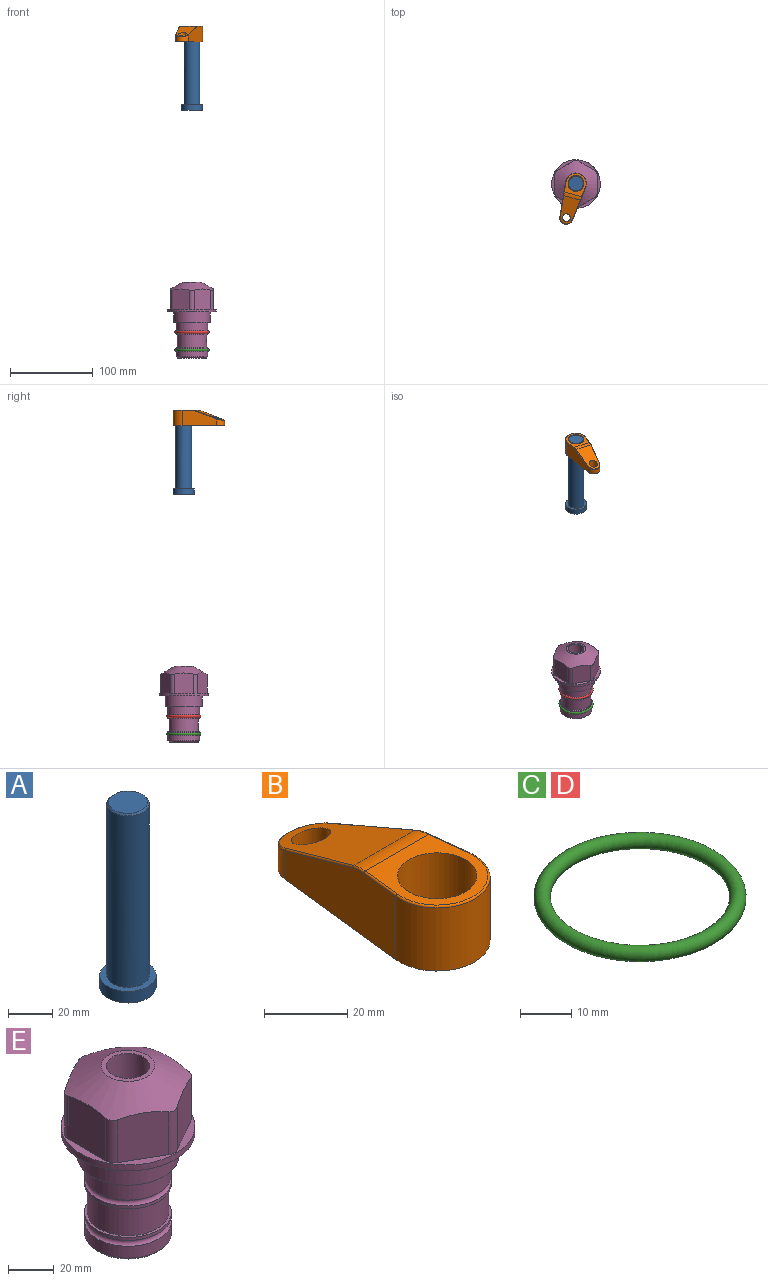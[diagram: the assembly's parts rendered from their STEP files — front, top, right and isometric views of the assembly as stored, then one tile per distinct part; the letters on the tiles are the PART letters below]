
ASSEMBLY  parts=5 mates=3
PART A: 6 faces, bbox 25.4x25.4x101.6 mm
  f0: plane 17.46x17.46mm, normal (0,0,1), area 239.5mm2, adj f5
  f1: plane 25.4x25.4mm, normal (0,0,-1), area 506.7mm2, adj f2
  f2: cylinder r=12.7mm len=25.4mm, axis (0,0,1), area 506.7mm2, adj f1,f3
  f3: plane 25.4x25.4mm, normal (0,0,1), area 221.7mm2, adj f2,f4
  f4: cylinder r=9.53mm len=94.46mm, axis (0,0,1), area 5653mm2, adj f3,f5
  f5: cone r=8.73mm half-angle=45deg, axis (0,0,-1), area 64.4mm2, adj f0,f4
PART B: 44 faces, bbox 27.5x64.5x19.1 mm
  f0: plane 2.3x0.95mm, normal (0,0,-1), area 1mm2, adj f25,f30,f34
  f1: plane 63.5x25.4mm, normal (0,0,-1), area 561.7mm2, adj f2,f3,f4,f5,f6,f7,f19,f20
  f2: cylinder r=12.7mm len=25.4mm, axis (0,0,-1), area 792.2mm2, adj f1,f3,f5,f13
  f3: plane 42.33x18.54mm, normal (0.99,0.11,0), area 647mm2, adj f1,f2,f4,f11,f12,f14
  f4: cylinder r=7.94mm len=15.78mm, axis (0,0,-1), area 158.6mm2, adj f1,f3,f5,f16
  f5: plane 42.33x18.54mm, normal (-0.99,0.11,0), area 647mm2, adj f1,f2,f4,f15,f17,f18
  f6: cylinder r=9.53mm len=19.05mm, axis (0,0,-1), area 1140.1mm2, adj f1,f8
  f7: cylinder r=4.76mm len=10.98mm, axis (0,0,-1), area 276.1mm2, adj f1,f9
  f8: plane 25.83x24.38mm, normal (0,0,1), area 262.2mm2, adj f6,f10,f11,f13,f15
  f9: plane 32.49x20.55mm, normal (0,0.34,0.94), area 489.9mm2, adj f7,f10,f14,f16,f18
  f10: cylinder r=12.7mm len=21.49mm, axis (-1,0,0), area 93.2mm2, adj f8,f9,f12,f17
  f11: cylinder r=0.51mm len=12.34mm, axis (0.11,-0.99,0), area 9.9mm2, adj f3,f8,f12,f13
  f12: bspline ~7.62x1.64mm, area 3.5mm2, adj f3,f10,f11,f14
  f13: torus R=12.19mm, axis (0,0,1), area 33.6mm2, adj f2,f8,f11,f15
  f14: cylinder r=0.51mm len=26.01mm, axis (0.1,-0.93,0.34), area 21.6mm2, adj f3,f9,f12,f16
  f15: cylinder r=0.51mm len=12.34mm, axis (0.11,0.99,0), area 9.9mm2, adj f5,f8,f13,f17
  f16: bspline ~15.78x7.05mm, area 15.7mm2, adj f4,f9,f14,f18
  f17: bspline ~7.62x1.64mm, area 3.5mm2, adj f5,f10,f15,f18
  f18: cylinder r=0.51mm len=26.01mm, axis (0.1,0.93,-0.34), area 21.6mm2, adj f5,f9,f16,f17
  f19: plane 21.6x14.29mm, normal (-0.99,-0.11,0), area 242.6mm2, adj f1,f26,f28,f34,f36,f38
  f20: plane 21.6x14.29mm, normal (0.99,-0.11,0), area 242.6mm2, adj f1,f27,f29,f37,f39,f41
  f21: cylinder r=12.7mm len=14.29mm, axis (0,0,-1), area 173.2mm2, adj f1,f26,f27,f30,f31,f33
  f22: cylinder r=7.94mm len=7.63mm, axis (0,0,-1), area 53.8mm2, adj f1,f28,f29,f42
  f23: plane 2.3x0.95mm, normal (0,0,-1), area 1mm2, adj f25,f33,f37
  f24: plane 17.94x12.32mm, normal (0,-0.34,-0.94), area 191.2mm2, adj f25,f38,f41,f42
  f25: cylinder r=9.53mm len=12.93mm, axis (-1,0,0), area 37.5mm2, adj f0,f23,f24,f31,f36,f39
  f26: cylinder r=1.59mm len=14.29mm, axis (0,0,-1), area 49mm2, adj f1,f19,f21,f32
  f27: cylinder r=1.59mm len=14.29mm, axis (0,0,-1), area 49mm2, adj f1,f20,f21,f35
  f28: cylinder r=1.59mm len=7.28mm, axis (0,0,-1), area 22.1mm2, adj f1,f19,f22,f40
  f29: cylinder r=1.59mm len=7.28mm, axis (0,0,-1), area 22.1mm2, adj f1,f20,f22,f43
  f30: torus R=14.29mm, axis (0,0,1), area 5.8mm2, adj f0,f21,f31,f32
  f31: bspline ~11.06x2.73mm, area 20.8mm2, adj f21,f25,f30,f33
  f32: sphere r=1.59mm, area 5.4mm2, adj f26,f30,f34
  f33: torus R=14.29mm, axis (0,0,1), area 5.8mm2, adj f21,f23,f31,f35
  f34: cylinder r=1.59mm len=1.68mm, axis (-0.11,0.99,0), area 2.4mm2, adj f0,f19,f32,f36
  f35: sphere r=1.59mm, area 5.4mm2, adj f27,f33,f37
  f36: bspline ~5.82x2.33mm, area 7.7mm2, adj f19,f25,f34,f38
  f37: cylinder r=1.59mm len=1.68mm, axis (0.11,0.99,0), area 2.4mm2, adj f20,f23,f35,f39
  f38: cylinder r=1.59mm len=18.33mm, axis (0.1,-0.93,0.34), area 46.7mm2, adj f19,f24,f36,f40
  f39: bspline ~5.82x2.33mm, area 7.7mm2, adj f20,f25,f37,f41
  f40: sphere r=1.59mm, area 3.6mm2, adj f28,f38,f42
  f41: cylinder r=1.59mm len=18.33mm, axis (0.1,0.93,-0.34), area 46.7mm2, adj f20,f24,f39,f43
  f42: bspline ~8.31x1.84mm, area 15.3mm2, adj f22,f24,f40,f43
  f43: sphere r=1.59mm, area 3.6mm2, adj f29,f41,f42
PART C: 1 faces, bbox 44.7x44.7x3.2 mm
  f0: torus R=19.05mm, axis (0,0,1), area 1193.9mm2
PART D: same geometry as C
PART E: 36 faces, bbox 58.7x58.7x91.2 mm
  f0: cylinder r=17.78mm len=35.56mm, axis (0,0,1), area 1670.8mm2, adj f23,f24,f31
  f1: cylinder r=19.05mm len=38.1mm, axis (0,0,1), area 1191.9mm2, adj f26,f27,f30
  f2: plane 58.66x58.66mm, normal (0,0,-1), area 1150.6mm2, adj f3,f28
  f3: cylinder r=29.33mm len=58.66mm, axis (0,0,-1), area 585.1mm2, adj f2,f4
  f4: plane 58.66x58.66mm, normal (0,0,1), area 475.9mm2, adj f3,f5,f6,f7,f8,f9,f10,f11
  f5: plane 24.5x20.32mm, normal (-0.5,0.87,0), area 562.8mm2, adj f4,f15,f16,f17
  f6: plane 24.5x20.32mm, normal (0.5,0.87,0), area 562.8mm2, adj f4,f14,f15,f17
  f7: plane 24.5x23.48mm, normal (1,0,0), area 562.8mm2, adj f4,f13,f14,f17
  f8: plane 24.5x20.32mm, normal (0.5,-0.87,0), area 562.8mm2, adj f4,f12,f13,f17
  f9: plane 24.5x20.32mm, normal (-0.5,-0.87,0), area 562.8mm2, adj f4,f11,f12,f17
  f10: plane 24.5x23.48mm, normal (-1,0,0), area 562.8mm2, adj f4,f11,f16,f17
  f11: cylinder r=5.08mm len=23.01mm, axis (0,0,-1), area 121.2mm2, adj f4,f9,f10,f17
  f12: cylinder r=5.08mm len=23.01mm, axis (0,0,-1), area 121.2mm2, adj f4,f8,f9,f17
  f13: cylinder r=5.08mm len=23.01mm, axis (0,0,-1), area 121.2mm2, adj f4,f7,f8,f17
  f14: cylinder r=5.08mm len=23.01mm, axis (0,0,-1), area 121.2mm2, adj f4,f6,f7,f17
  f15: cylinder r=5.08mm len=23.01mm, axis (0,0,-1), area 121.2mm2, adj f4,f5,f6,f17
  f16: cylinder r=5.08mm len=23.01mm, axis (0,0,-1), area 121.2mm2, adj f4,f5,f10,f17
  f17: cone r=11.73mm half-angle=60deg, axis (0,0,-1), area 2071.8mm2, adj f5,f6,f7,f8,f9,f10,f11,f12
  f18: plane 23.46x23.46mm, normal (0,0,1), area 147.4mm2, adj f17,f35
  f19: plane 34.93x34.93mm, normal (0,0,-1), area 958mm2, adj f29
  f20: cylinder r=19.05mm len=38.1mm, axis (0,0,1), area 760.1mm2, adj f21,f29
  f21: torus R=19.05mm, axis (0,0,1), area 565.3mm2, adj f20,f22
  f22: cylinder r=19.05mm len=38.1mm, axis (0,0,1), area 190mm2, adj f21,f23
  f23: plane 38.1x38.1mm, normal (0,0,1), area 146.9mm2, adj f0,f22
  f24: plane 38.1x38.1mm, normal (0,0,-1), area 146.9mm2, adj f0,f25
  f25: cylinder r=19.05mm len=38.1mm, axis (0,0,1), area 190mm2, adj f24,f26
  f26: torus R=19.05mm, axis (0,0,1), area 565.3mm2, adj f1,f25
  f27: plane 44.45x44.45mm, normal (0,0,-1), area 411.7mm2, adj f1,f28
  f28: cylinder r=22.23mm len=44.45mm, axis (0,0,1), area 1773.5mm2, adj f2,f27
  f29: cone r=19.05mm half-angle=45deg, axis (0,0,1), area 257.5mm2, adj f19,f20
  f30: cylinder r=3.17mm len=6.75mm, axis (-1,0,0), area 128mm2, adj f1,f33
  f31: cylinder r=3.17mm len=6.35mm, axis (-1,0,0), area 102.5mm2, adj f0,f33
  f32: plane 25.4x25.4mm, normal (0,0,1), area 506.7mm2, adj f33
  f33: cylinder r=12.7mm len=66.42mm, axis (0,0,-1), area 5236.2mm2, adj f30,f31,f32,f34
  f34: cone r=9.53mm half-angle=30deg, axis (0,0,-1), area 443.4mm2, adj f33,f35
  f35: cylinder r=9.53mm len=19.05mm, axis (0,0,-1), area 849mm2, adj f18,f34
PLACE A rot(axis=(0,0,-1),105.7deg) t=(0,0,271.23)mm
PLACE B rot(axis=(0,0,1),164.3deg) t=(0,0,325.84)mm
PLACE C t=(0,0,-21.59)mm
PLACE D at identity
PLACE E at identity fixed
MATE fastened C.f0 <-> E.f0  axis (0,0,1) through (0,0,-46.1)mm
MATE cylindrical A.f2 <-> E.f0  axis (0,0,1) through (0,0,296.87)mm
MATE fastened B.f2 <-> A.f2  axis (0,0,1) through (0,0,344.89)mm
